# Revit family: Hager-Golf-IP40-Transparent_Door-syst-NoHosted-DE-de
name_source: partatom
category: Electrical Equipment
units: mm (PartAtom-declared; Revit-internal decimal feet)

## family parameters
Always vertical = Yes
Cut with Voids When Loaded = No
Panel Configuration = Two Columns, Circuits Across
Part Type = Panelboard
Room Calculation Point = No
Round Connector Dimension = Use Diameter
Shared = No
Work Plane-Based = Yes

## types (2) — shared parameters
Default Elevation = 1219 mm
EF000003 - Montageart = EV000383 - Unterputz
EF000007 - Farbe = EV000202 - weiß
EF000008 - Breite = 275 mm
EF000040 - Höhe = 225 mm  [stored 0.738189 ft]
EF000049 - Tiefe = 98 mm  [stored 0.321522 ft]
EF000116 - RAL-Nummer = 9010
EF000118 - Mit Montageplatte = No
EF000218 - Einbautiefe = 72 mm  [stored 0.23622 ft]
EF000266 - Anzahl der Reihen = 1
EF000332 - Einbauhöhe = 189 mm  [stored 0.620079 ft]
EF000339 - Art der Abdeckung = EV004216 - Tür
EF000846 - Einbaubreite = 242 mm  [stored 0.793963 ft]
EF001062 - EMV-Ausführung = No
EF001088 - Anbaumöglichkeit = Yes
EF001131 - Innentiefe = 98 mm  [stored 0.321522 ft]
EF001134 - DIN-Schiene = Yes
EF001596 - Werkstoff des Gehäuses = EV000139 - Kunststoff
EF002950 - Breite in Teilungseinheiten = 8
EF004462 - Art der Schließung = EV000154 - sonstige
EF006244 - Transparenter Deckel/Tür = Yes
EF006306 - Mit Schloss = No
EF009212 - Ausführung Deckel = EV000116 - geschlossen
EF015776 - Erdungsklemmenblock = Yes
EF015777 - Neutralleiterklemmenblock = Yes
EF015941 - Signaldurchlassende Tür = Yes
HG000001 - Anzahl der Spalten = 1
HG000002 - Mit tür = Yes
HG000003 - Bereich = Golf
HG000005 - Dicke = 3 mm  [stored 0.00984252 ft]
HG000006 - Unterputz = Yes
HG000009 - Doppelflügeligen Tür = No
HG000010 - Asymmetrische Türen = No
HG000011 - Leere Reihen von unten = No
HG000017 - Distanz zwischen den Polen = 18 mm  [stored 0.0590551 ft]
Manufacturer = Hager
Type Comments = Golf
zero-valued in all types: HG000007 - Anzahl der leeren Spalten, HG000008 - Anzahl der leeren Reihen

## per-type parameters (varying)
| type | HG000004 - Herstellerreferenz | Model |
| Unterputz  B275 H225 T97.5 8 Teilungseinheiten - VF108TA | VF108TA | VF108TA |
| Unterputz  B275 H225 T97.5 8 Teilungseinheiten - VF108TT | VF108TT | VF108TT |

note: [stored X ft] marks values corroborated as IEEE doubles in the binary element streams (Revit-internal decimal feet)

## geometry (parser evidence)
native form markers: Sweep x13
no freeform markers — native parametric forms only
